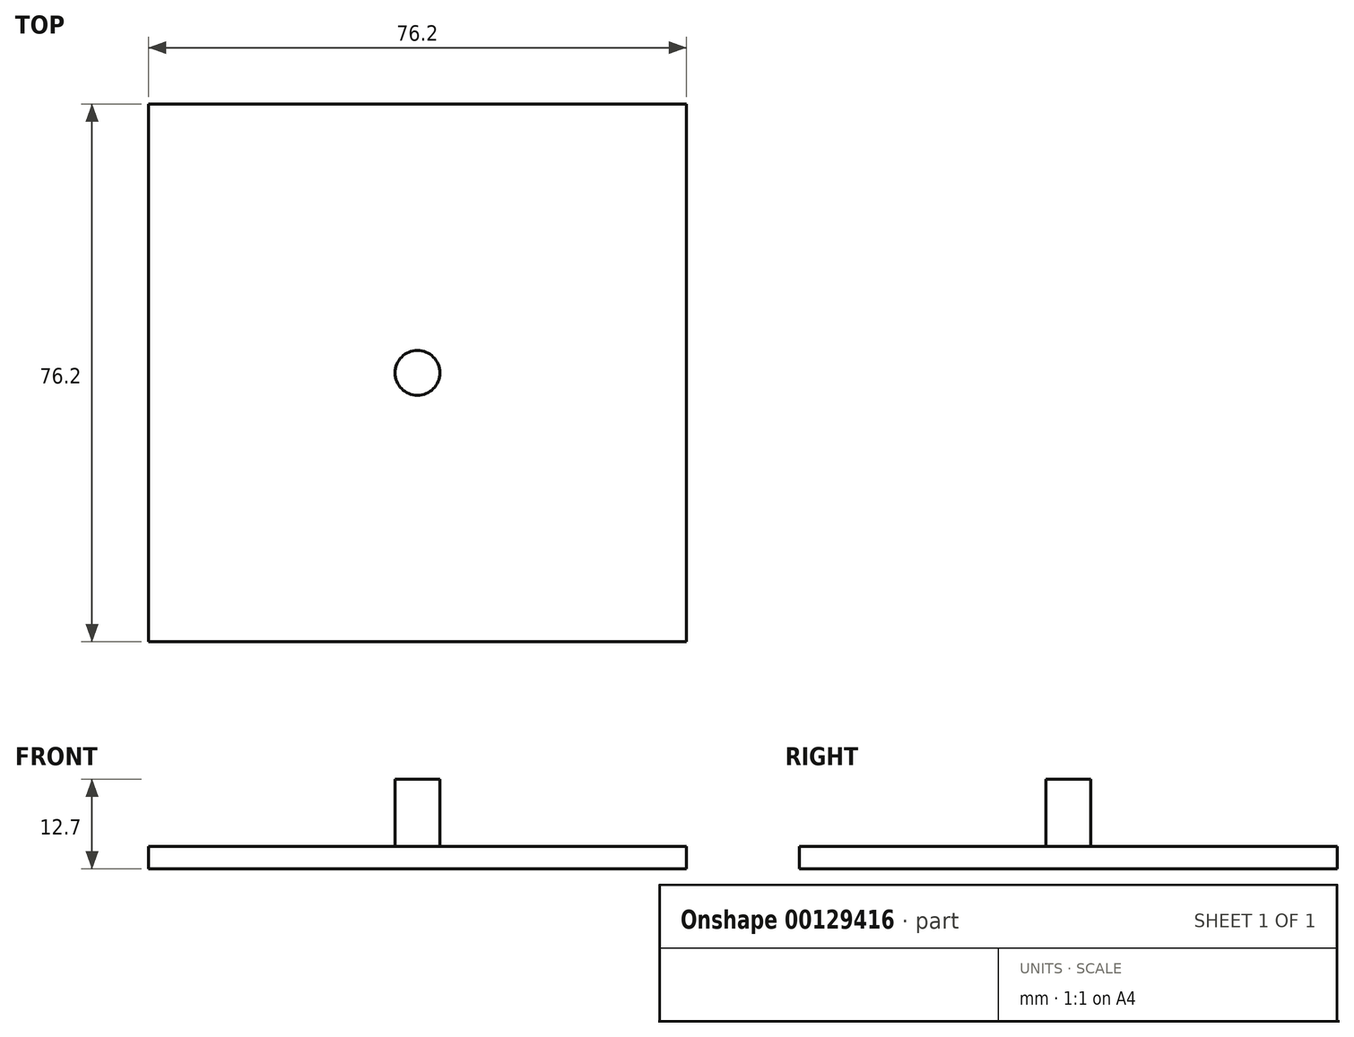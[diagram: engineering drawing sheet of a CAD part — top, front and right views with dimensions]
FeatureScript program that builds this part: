
annotation { "Feature Type Name" : "Feature", "Feature Type Description" : "" }
export const myFeature = defineFeature(function(context is Context, id is Id, definition is map)
    precondition{}
    {
        {
            var Q0;
            Q0=qCreatedBy(makeId("Top.planeOp"),FACE);
            var sketch = newSketch(context, id + "F0", { "sketchPlane" : qUnion([Q0])});
            skCircle(sketch, "E0", {"center": v(0, 0) * mm, "radius": 3.18 * mm});
            skSolve(sketch);
        }
        {
            var Q0;
            Q0 = qSketchRegion(id + "F0", true);
            extrude(context, id + "F1", {"entities" : qUnion([Q0]), "depth" : 12.7 * mm});
        }
        {
            var Q0;
            Q0=qCreatedBy(makeId("Top.planeOp"),FACE);
            var sketch = newSketch(context, id + "F2", { "sketchPlane" : qUnion([Q0])});
            skLineSegment(sketch, "E1.bottom", {"start": v(38.1, -38.1) * mm, "end": v(-38.1, -38.1) * mm});
            skLineSegment(sketch, "E1.top", {"start": v(38.1, 38.1) * mm, "end": v(-38.1, 38.1) * mm});
            skLineSegment(sketch, "E1.left", {"start": v(38.1, -38.1) * mm, "end": v(38.1, 38.1) * mm});
            skLineSegment(sketch, "E1.right", {"start": v(-38.1, -38.1) * mm, "end": v(-38.1, 38.1) * mm});
            skPoint(sketch, "E1.middle", {"position": v(0, 0) * mm});
            skSolve(sketch);
        }
        {
            var Q0;
            Q0 = qSketchRegion(id + "F2", true);
            extrude(context, id + "F3", {"entities" : qUnion([Q0]), "operationType" : NewBodyOperationType.ADD, "depth" : 3.17 * mm});
        }
    });
